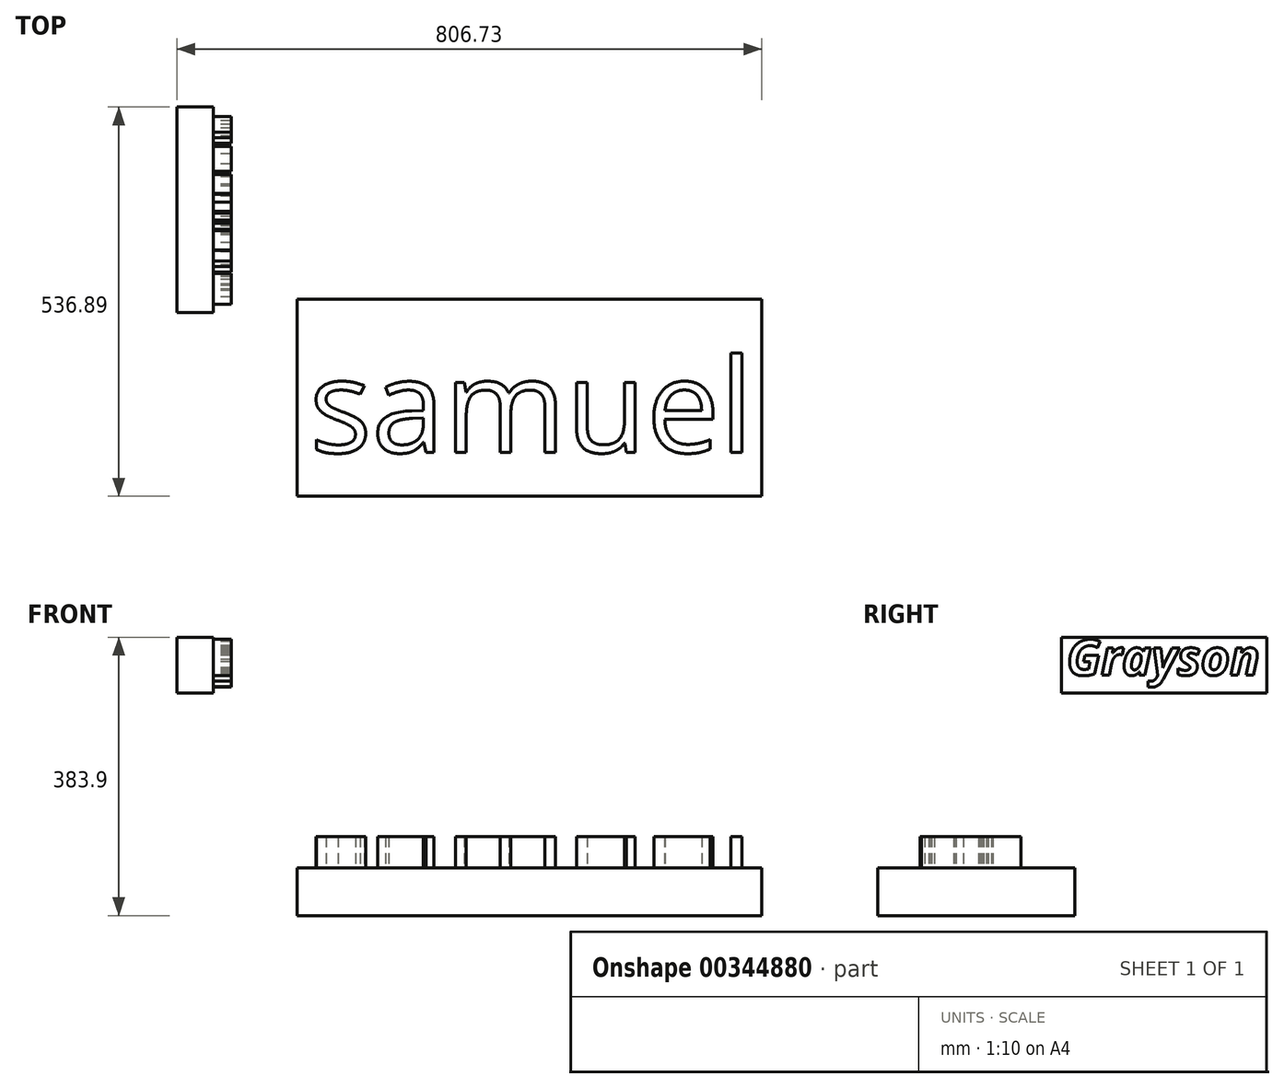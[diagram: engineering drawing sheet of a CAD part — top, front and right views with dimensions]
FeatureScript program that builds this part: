
annotation { "Feature Type Name" : "Feature", "Feature Type Description" : "" }
export const myFeature = defineFeature(function(context is Context, id is Id, definition is map)
    precondition{}
    {
        {
            var Q0;
            Q0=qCreatedBy(makeId("Front.planeOp"),FACE);
            var sketch = newSketch(context, id + "F0", { "sketchPlane" : qUnion([Q0])});
            skLineSegment(sketch, "E0.bottom", {"start": v(806.73, -66.07) * mm, "end": v(166.17, -66.07) * mm});
            skLineSegment(sketch, "E0.top", {"start": v(806.73, 0) * mm, "end": v(166.17, 0) * mm});
            skLineSegment(sketch, "E0.left", {"start": v(806.73, -66.07) * mm, "end": v(806.73, 0) * mm});
            skLineSegment(sketch, "E0.right", {"start": v(166.17, -66.07) * mm, "end": v(166.17, 0) * mm});
            skSolve(sketch);
        }
        {
            var Q0;
            Q0=makeQuery(id+"F0.imprint","IMPRINT",FACE,{"disambiguationData":[TD([[makeQuery(id+"F0.imprint","IMPRINT",EDGE,{"derivedFrom":sQuery(id+"F0.wireOp",EDGE,"E0.bottom")}),-1.0]])]});
            extrude(context, id + "F1", {"entities" : qUnion([Q0]), "depth" : 271.78 * mm});
        }
        {
            var Q0;
            Q0=makeQuery(id+"F1.opExtrude","SWEPT_FACE",FACE,{"disambiguationData":[OSD([sQuery(id+"F0.wireOp",EDGE,"E0.top")])]});
            var sketch = newSketch(context, id + "F2", { "sketchPlane" : qUnion([Q0])});
            skText(sketch, "E1", { "text": "samuel", "fontName": "OpenSans-Regular.ttf"});
            const initialGuessF2  = {"E1": [0.1828, -0.21144, 1, 0, 0.12991]};
            skSetInitialGuess(sketch, initialGuessF2);
            skSolve(sketch);
        }
        {
            var Q0;
            Q0 = qSketchRegion(id + "F2", true);
            extrude(context, id + "F3", {"entities" : qUnion([Q0]), "operationType" : NewBodyOperationType.ADD, "depth" : 43.18 * mm});
        }
        {
            var Q0;
            Q0=qCreatedBy(makeId("Right.planeOp"),FACE);
            var sketch = newSketch(context, id + "F4", { "sketchPlane" : qUnion([Q0])});
            skLineSegment(sketch, "E2.bottom", {"start": v(222.19, 261.58) * mm, "end": v(34.3, 261.58) * mm});
            skLineSegment(sketch, "E2.top", {"start": v(222.19, 317.83) * mm, "end": v(34.3, 317.83) * mm});
            skLineSegment(sketch, "E2.left", {"start": v(222.19, 261.58) * mm, "end": v(222.19, 317.83) * mm});
            skLineSegment(sketch, "E2.right", {"start": v(34.3, 261.58) * mm, "end": v(34.3, 317.83) * mm});
            skSolve(sketch);
        }
        {
            var Q0;
            Q0=makeQuery(id+"F4.imprint","IMPRINT",FACE,{"disambiguationData":[TD([[makeQuery(id+"F4.imprint","IMPRINT",EDGE,{"derivedFrom":sQuery(id+"F4.wireOp",EDGE,"E2.bottom")}),-1.0]])]});
            extrude(context, id + "F5", {"entities" : qUnion([Q0]), "depth" : 50.8 * mm});
        }
        {
            var Q0;
            Q0=makeQuery(id+"F5.opExtrude","CAP_FACE",FACE,{"disambiguationData":[OSD([sQuery(id+"F4.wireOp",EDGE,"E2.bottom"),sQuery(id+"F4.wireOp",EDGE,"E2.top"),sQuery(id+"F4.wireOp",EDGE,"E2.left"),sQuery(id+"F4.wireOp",EDGE,"E2.right")])],"isStart":false});
            var sketch = newSketch(context, id + "F6", { "sketchPlane" : qUnion([Q0])});
            skText(sketch, "E3", { "text": "Grayson", "fontName": "OpenSans-BoldItalic.ttf"});
            const initialGuessF6  = {"E3": [-0.01125, 0.26552, 1, 0, 0.04937]};
            skSetInitialGuess(sketch, initialGuessF6);
            skSolve(sketch);
        }
        {
            var Q0;
            Q0=makeQuery(id+"F5.opExtrude","SWEPT_FACE",FACE,{"disambiguationData":[OSD([sQuery(id+"F4.wireOp",EDGE,"E2.right")])]});
            extrude(context, id + "F7", {"entities" : qUnion([Q0]), "operationType" : NewBodyOperationType.ADD, "depth" : 52.58 * mm});
        }
        {
            var Q0;
            Q0=makeQuery(id+"F5.opExtrude","SWEPT_FACE",FACE,{"disambiguationData":[OSD([sQuery(id+"F4.wireOp",EDGE,"E2.left")])]});
            extrude(context, id + "F8", {"entities" : qUnion([Q0]), "operationType" : NewBodyOperationType.ADD, "depth" : 42.93 * mm});
        }
        {
            var Q0;
            {var subQ0=sQuery(id+"F4.wireOp",EDGE,"E2.bottom");Q0=makeQuery(id+"F8.boolean.opBoolean","MERGE",FACE,{"derivedFrom":[makeQuery(id+"F7.boolean.opBoolean","MERGE",FACE,{"derivedFrom":[makeQuery(id+"F5.opExtrude","SWEPT_FACE",FACE,{"disambiguationData":[OSD([subQ0])]}),makeQuery(id+"F7.opExtrude","SWEPT_FACE",FACE,{"disambiguationData":[OSD([subQ0,sQuery(id+"F4.wireOp",EDGE,"E2.right")])]})]}),makeQuery(id+"F8.opExtrude","SWEPT_FACE",FACE,{"disambiguationData":[OSD([subQ0,sQuery(id+"F4.wireOp",EDGE,"E2.left")])]})]});}
            extrude(context, id + "F9", {"entities" : qUnion([Q0]), "operationType" : NewBodyOperationType.ADD, "depth" : 20.83 * mm});
        }
        {
            var Q0;
            Q0 = qSketchRegion(id + "F6", true);
            extrude(context, id + "F10", {"entities" : qUnion([Q0]), "operationType" : NewBodyOperationType.ADD, "depth" : 24.64 * mm});
        }
    });
